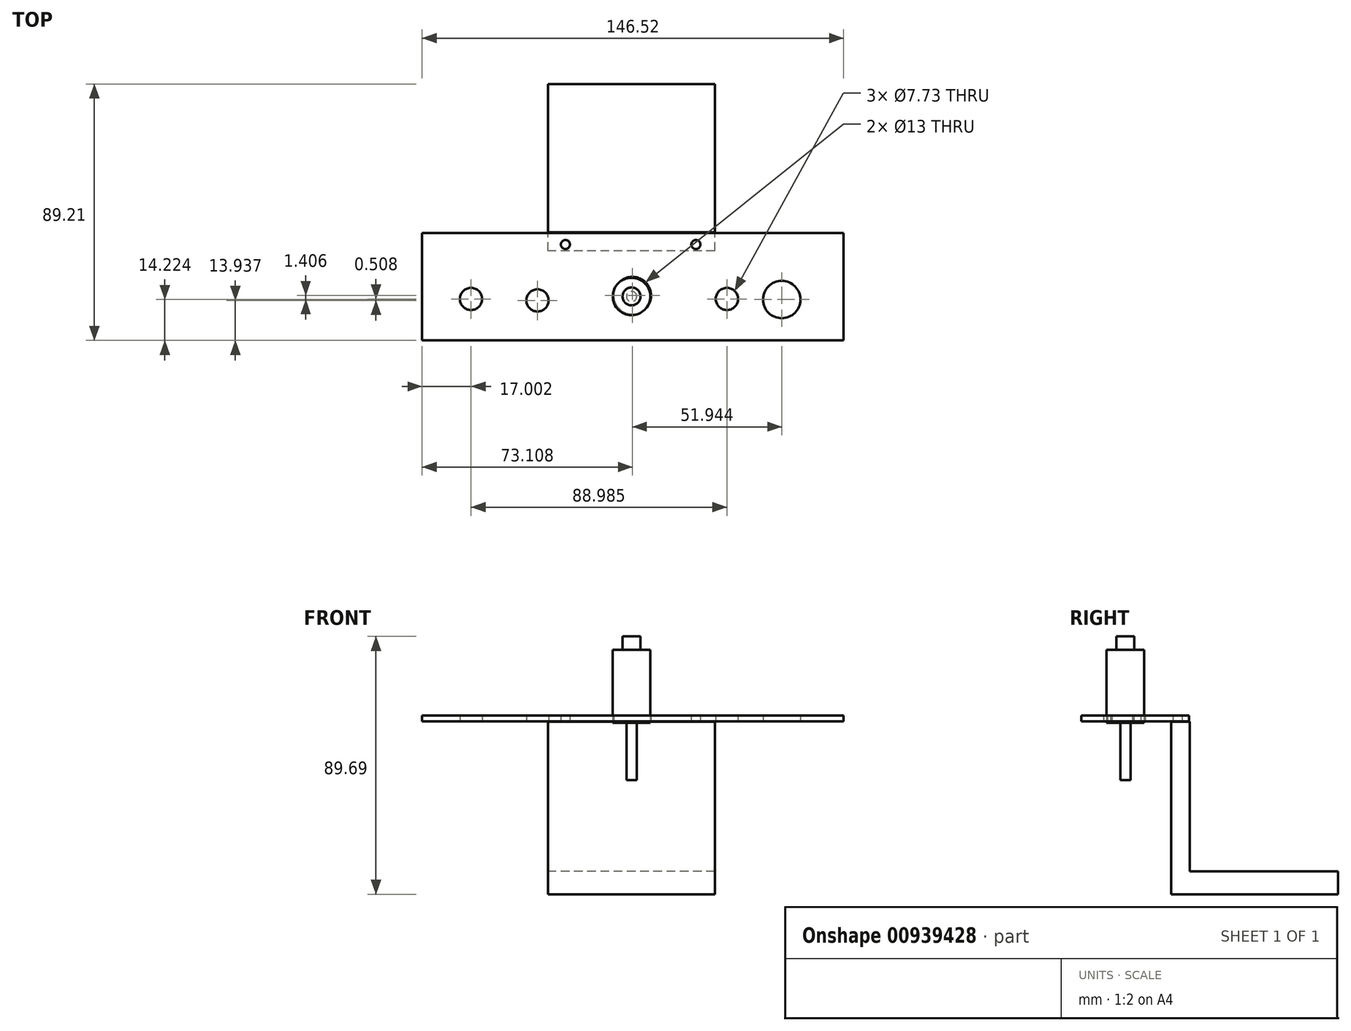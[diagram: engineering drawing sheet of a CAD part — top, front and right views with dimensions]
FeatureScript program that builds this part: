
annotation { "Feature Type Name" : "Feature", "Feature Type Description" : "" }
export const myFeature = defineFeature(function(context is Context, id is Id, definition is map)
    precondition{}
    {
        {
            var Q0;
            Q0=qCreatedBy(makeId("Top.planeOp"),FACE);
            var sketch = newSketch(context, id + "F0", { "sketchPlane" : qUnion([Q0])});
            skLineSegment(sketch, "E0.bottom", {"start": v(29, -29.86) * mm, "end": v(-29, -29.86) * mm});
            skLineSegment(sketch, "E0.top", {"start": v(29, 28.14) * mm, "end": v(-29, 28.14) * mm});
            skLineSegment(sketch, "E0.left", {"start": v(29, -29.86) * mm, "end": v(29, 28.14) * mm});
            skLineSegment(sketch, "E0.right", {"start": v(-29, -29.86) * mm, "end": v(-29, 28.14) * mm});
            skPoint(sketch, "E0.middle", {"position": v(0, -0.86) * mm});
            skLineSegment(sketch, "E1.bottom", {"start": v(-29, -24.89) * mm, "end": v(29, -24.89) * mm});
            skLineSegment(sketch, "E1.top", {"start": v(-29, -29.86) * mm, "end": v(29, -29.86) * mm});
            skLineSegment(sketch, "E1.left", {"start": v(-29, -24.89) * mm, "end": v(-29, -29.86) * mm});
            skLineSegment(sketch, "E1.right", {"start": v(29, -24.89) * mm, "end": v(29, -29.86) * mm});
            skLineSegment(sketch, "E2.bottom", {"start": v(-73.01, -23.4) * mm, "end": v(73.5, -23.4) * mm});
            skLineSegment(sketch, "E2.top", {"start": v(-73.01, -60.77) * mm, "end": v(73.5, -60.77) * mm});
            skLineSegment(sketch, "E2.left", {"start": v(-73.01, -23.4) * mm, "end": v(-73.01, -60.77) * mm});
            skLineSegment(sketch, "E2.right", {"start": v(73.5, -23.4) * mm, "end": v(73.5, -60.77) * mm});
            skCircle(sketch, "E3", {"center": v(22.18, -27.38) * mm, "radius": 1.58 * mm});
            skCircle(sketch, "E4", {"center": v(-23.17, -27.38) * mm, "radius": 1.58 * mm});
            skCircle(sketch, "E5", {"center": v(-56, -46.33) * mm, "radius": 3.87 * mm});
            skCircle(sketch, "E6", {"center": v(0.1, -45.14) * mm, "radius": 6.5 * mm});
            skCircle(sketch, "E7", {"center": v(-32.9, -46.83) * mm, "radius": 3.87 * mm});
            skCircle(sketch, "E8", {"center": v(52.04, -46.55) * mm, "radius": 6.5 * mm});
            skCircle(sketch, "E9", {"center": v(32.98, -46.33) * mm, "radius": 3.87 * mm});
            skSolve(sketch);
        }
        {
            var Q0;
            {var subQ0=sQuery(id+"F0.wireOp",EDGE,"E0.top");Q0=makeQuery(id+"F0.imprint","IMPRINT",FACE,{"disambiguationData":[TD([[makeQuery(id+"F0.imprint","IMPRINT",EDGE,{"derivedFrom":subQ0}),1.0]])]});}
            var Q1;
            Q1=makeQuery(id+"F0.imprint","IMPRINT",FACE,{"disambiguationData":[TD([[makeQuery(id+"F0.imprint","IMPRINT",EDGE,{"derivedFrom":sQuery(id+"F0.wireOp",EDGE,"E1.bottom")}),-1.0]])]});
            var Q2;
            Q2=makeQuery(id+"F0.imprint","IMPRINT",FACE,{"disambiguationData":[TD([[makeQuery(id+"F0.imprint","IMPRINT",EDGE,{"derivedFrom":sQuery(id+"F0.wireOp",EDGE,"E4")}),1.0]])]});
            var Q3;
            {var subQ0=sQuery(id+"F0.wireOp",EDGE,"E1.bottom");Q3=makeQuery(id+"F0.imprint","IMPRINT",FACE,{"disambiguationData":[TD([[makeQuery(id+"F0.imprint","IMPRINT",EDGE,{"derivedFrom":subQ0}),1.0]])]});}
            var Q4;
            Q4=makeQuery(id+"F0.imprint","IMPRINT",FACE,{"disambiguationData":[TD([[makeQuery(id+"F0.imprint","IMPRINT",EDGE,{"derivedFrom":sQuery(id+"F0.wireOp",EDGE,"E3")}),1.0]])]});
            extrude(context, id + "F1", {"entities" : qUnion([Q0, Q1, Q2, Q3, Q4]), "depth" : 8 * mm, "offsetDistance" : 25.4 * mm});
        }
        {
            var Q0;
            Q0=makeQuery(id+"F0.imprint","IMPRINT",FACE,{"disambiguationData":[TD([[makeQuery(id+"F0.imprint","IMPRINT",EDGE,{"derivedFrom":sQuery(id+"F0.wireOp",EDGE,"E1.bottom")}),-1.0]])]});
            var Q1;
            {var subQ0=sQuery(id+"F0.wireOp",EDGE,"E1.bottom");Q1=makeQuery(id+"F0.imprint","IMPRINT",FACE,{"disambiguationData":[TD([[makeQuery(id+"F0.imprint","IMPRINT",EDGE,{"derivedFrom":subQ0}),1.0]])]});}
            var Q2;
            Q2=makeQuery(id+"F0.imprint","IMPRINT",FACE,{"disambiguationData":[TD([[makeQuery(id+"F0.imprint","IMPRINT",EDGE,{"derivedFrom":sQuery(id+"F0.wireOp",EDGE,"E3")}),1.0]])]});
            var Q3;
            Q3=makeQuery(id+"F0.imprint","IMPRINT",FACE,{"disambiguationData":[TD([[makeQuery(id+"F0.imprint","IMPRINT",EDGE,{"derivedFrom":sQuery(id+"F0.wireOp",EDGE,"E4")}),1.0]])]});
            extrude(context, id + "F2", {"entities" : qUnion([Q0, Q1, Q2, Q3]), "operationType" : NewBodyOperationType.ADD, "depth" : 60 * mm, "offsetDistance" : 25.4 * mm});
        }
        {
            var Q0;
            Q0=qCreatedBy(makeId("Top.planeOp"),FACE);
            var sketch = newSketch(context, id + "F3", { "sketchPlane" : qUnion([Q0])});
            skPoint(sketch, "E10.middle", {"position": v(0, -35.2) * mm});
            skLineSegment(sketch, "E11.bottom", {"start": v(-72.82, 5.01) * mm, "end": v(73.7, 5.01) * mm});
            skLineSegment(sketch, "E11.top", {"start": v(-72.82, -32.37) * mm, "end": v(73.7, -32.37) * mm});
            skLineSegment(sketch, "E11.left", {"start": v(-72.82, 5.01) * mm, "end": v(-72.82, -32.37) * mm});
            skLineSegment(sketch, "E11.right", {"start": v(73.7, 5.01) * mm, "end": v(73.7, -32.37) * mm});
            skCircle(sketch, "E12", {"center": v(22.37, 1.03) * mm, "radius": 1.58 * mm});
            skCircle(sketch, "E13", {"center": v(-22.99, 1.03) * mm, "radius": 1.58 * mm});
            skCircle(sketch, "E14", {"center": v(-55.82, -17.92) * mm, "radius": 3.87 * mm});
            skCircle(sketch, "E15", {"center": v(0.29, -16.74) * mm, "radius": 6.5 * mm});
            skCircle(sketch, "E16", {"center": v(-32.7, -18.43) * mm, "radius": 3.87 * mm});
            skCircle(sketch, "E17", {"center": v(52.23, -18.14) * mm, "radius": 6.5 * mm});
            skCircle(sketch, "E18", {"center": v(33.17, -17.92) * mm, "radius": 3.87 * mm});
            skSolve(sketch);
        }
        {
            var Q0;
            Q0=makeQuery(id+"F3.imprint","IMPRINT",FACE,{"disambiguationData":[TD([[makeQuery(id+"F3.imprint","IMPRINT",EDGE,{"derivedFrom":sQuery(id+"F3.wireOp",EDGE,"E11.bottom")}),-1.0]])]});
            extrude(context, id + "F4", {"entities" : qUnion([Q0]), "depth" : 2 * mm, "offsetDistance" : 25.4 * mm});
        }
        {
            var Q0;
            Q0=makeQuery(id+"F4.opExtrude","SWEPT_BODY",BODY,{"disambiguationData":[OSD([sQuery(id+"F3.wireOp",EDGE,"E11.bottom"),sQuery(id+"F3.wireOp",EDGE,"E11.top"),sQuery(id+"F3.wireOp",EDGE,"E11.left"),sQuery(id+"F3.wireOp",EDGE,"E11.right"),sQuery(id+"F3.wireOp",EDGE,"E12"),sQuery(id+"F3.wireOp",EDGE,"E13"),sQuery(id+"F3.wireOp",EDGE,"E14"),sQuery(id+"F3.wireOp",EDGE,"E15"),sQuery(id+"F3.wireOp",EDGE,"E16"),sQuery(id+"F3.wireOp",EDGE,"E17"),sQuery(id+"F3.wireOp",EDGE,"E18")])]});
            transform(context, id + "F5", {"entities" : qUnion([Q0]), "transformType" : TransformType.TRANSLATION_3D, "dx" : 0 * mm, "dy" : -28.7 * mm, "dz" : 60.2 * mm, "makeCopy" : false});
        }
        {
            var Q0;
            Q0=qCreatedBy(makeId("Top.planeOp"),FACE);
            var sketch = newSketch(context, id + "F6", { "sketchPlane" : qUnion([Q0])});
            skCircle(sketch, "E19", {"center": v(0, -45.54) * mm, "radius": 6.52 * mm});
            skCircle(sketch, "E20", {"center": v(0, -45.54) * mm, "radius": 3.12 * mm});
            skCircle(sketch, "E21", {"center": v(0, -45.54) * mm, "radius": 1.8 * mm});
            skSolve(sketch);
        }
        {
            var Q0;
            Q0=makeQuery(id+"F6.imprint","IMPRINT",FACE,{"disambiguationData":[TD([[makeQuery(id+"F6.imprint","IMPRINT",EDGE,{"derivedFrom":sQuery(id+"F6.wireOp",EDGE,"E19")}),1.0]])]});
            var Q1;
            Q1=makeQuery(id+"F6.imprint","IMPRINT",FACE,{"disambiguationData":[TD([[makeQuery(id+"F6.imprint","IMPRINT",EDGE,{"derivedFrom":sQuery(id+"F6.wireOp",EDGE,"E20")}),1.0]])]});
            var Q2;
            Q2=makeQuery(id+"F6.imprint","IMPRINT",FACE,{"disambiguationData":[TD([[makeQuery(id+"F6.imprint","IMPRINT",EDGE,{"derivedFrom":sQuery(id+"F6.wireOp",EDGE,"E21")}),1.0]])]});
            extrude(context, id + "F7", {"entities" : qUnion([Q0, Q1, Q2]), "depth" : 25.4 * mm, "offsetDistance" : 25.4 * mm});
        }
        {
            var Q0;
            Q0=makeQuery(id+"F6.imprint","IMPRINT",FACE,{"disambiguationData":[TD([[makeQuery(id+"F6.imprint","IMPRINT",EDGE,{"derivedFrom":sQuery(id+"F6.wireOp",EDGE,"E21")}),1.0]])]});
            var Q1;
            Q1=makeQuery(id+"F6.imprint","IMPRINT",FACE,{"disambiguationData":[TD([[makeQuery(id+"F6.imprint","IMPRINT",EDGE,{"derivedFrom":sQuery(id+"F6.wireOp",EDGE,"E20")}),1.0]])]});
            extrude(context, id + "F8", {"entities" : qUnion([Q0, Q1]), "operationType" : NewBodyOperationType.ADD, "depth" : 30 * mm, "offsetDistance" : 25.4 * mm});
        }
        {
            var Q0;
            Q0=makeQuery(id+"F6.imprint","IMPRINT",FACE,{"disambiguationData":[TD([[makeQuery(id+"F6.imprint","IMPRINT",EDGE,{"derivedFrom":sQuery(id+"F6.wireOp",EDGE,"E21")}),1.0]])]});
            extrude(context, id + "F9", {"entities" : qUnion([Q0]), "operationType" : NewBodyOperationType.ADD, "depth" : -20 * mm, "offsetDistance" : 25.4 * mm});
        }
        {
            var Q0;
            Q0=makeQuery(id+"F7.opExtrude","SWEPT_BODY",BODY,{"disambiguationData":[OSD([sQuery(id+"F6.wireOp",EDGE,"E19")])]});
            transform(context, id + "F10", {"entities" : qUnion([Q0]), "transformType" : TransformType.TRANSLATION_3D, "dx" : 0 * mm, "dy" : -0.23 * mm, "dz" : 59.69 * mm, "makeCopy" : false});
        }
    });
